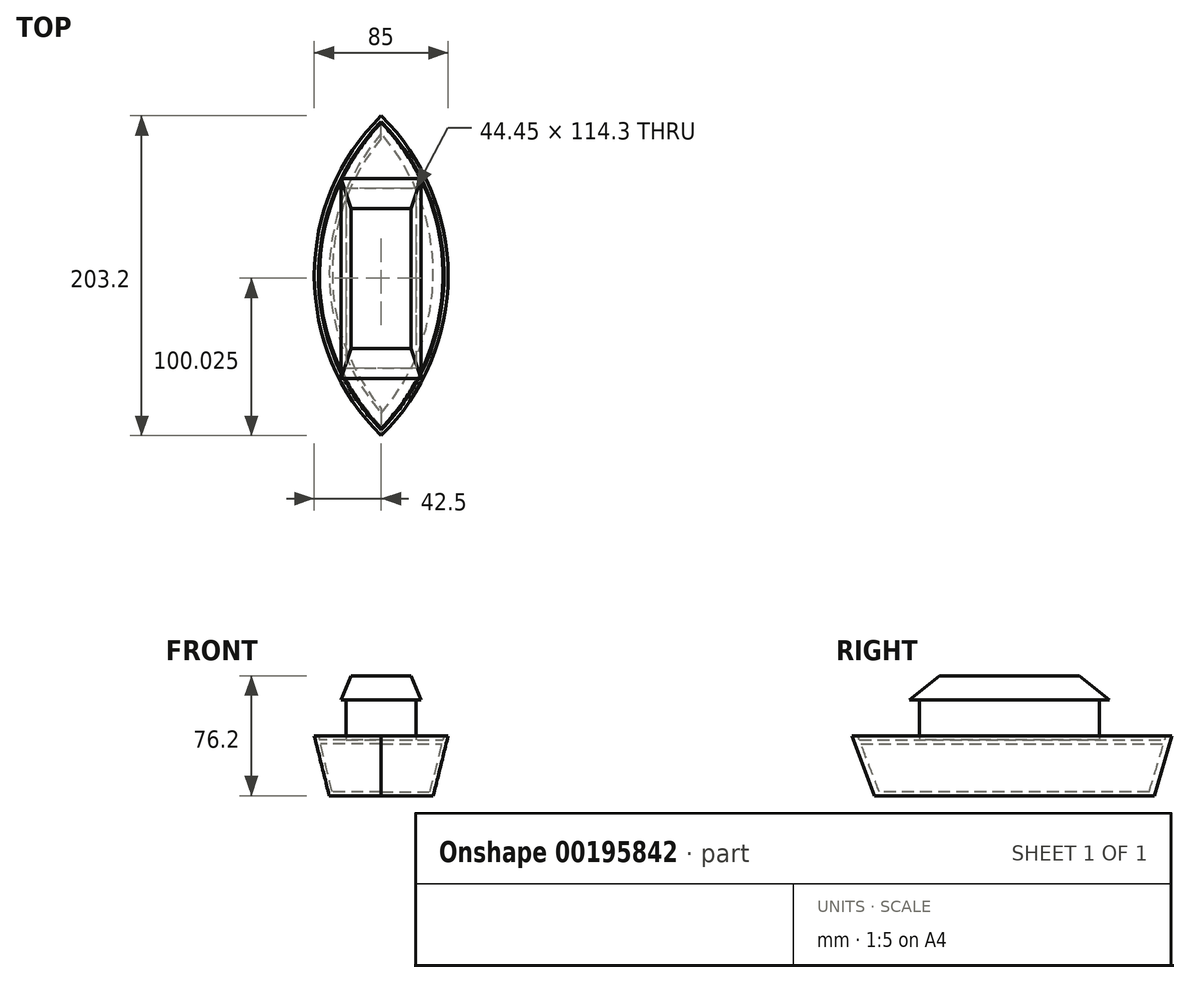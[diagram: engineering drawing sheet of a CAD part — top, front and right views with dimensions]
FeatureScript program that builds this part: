
annotation { "Feature Type Name" : "Feature", "Feature Type Description" : "" }
export const myFeature = defineFeature(function(context is Context, id is Id, definition is map)
    precondition{}
    {
        {
            var Q0;
            Q0=qCreatedBy(makeId("Top.planeOp"),FACE);
            var sketch = newSketch(context, id + "F0", { "sketchPlane" : qUnion([Q0])});
            skArc(sketch, "E0", {"start": v(0, -98.62) * mm, "mid": v(33.06, -9.72) * mm, "end": v(0, 79.18) * mm});
            skArc(sketch, "E1.MirrorCS", {"start": v(0, -98.62) * mm, "mid": v(-33.06, -9.72) * mm, "end": v(0, 79.18) * mm});
            skSolve(sketch);
        }
        {
            var Q0;
            Q0=qCreatedBy(makeId("Top.planeOp"),FACE);
            cPlane(context, id + "F1", {"entities" : qUnion([Q0]), "cplaneType" : CPlaneType.OFFSET, "offset" : 38.1 * mm, "width" : 152.4 * mm, "height" : 152.4 * mm});
        }
        {
            var Q0;
            Q0=qCreatedBy(id+"F1.planeOp",FACE);
            var sketch = newSketch(context, id + "F2", { "sketchPlane" : qUnion([Q0])});
            skArc(sketch, "E2", {"start": v(0, -112.85) * mm, "mid": v(42.5, -11.25) * mm, "end": v(0, 90.35) * mm});
            skArc(sketch, "E3.MirrorCS", {"start": v(0, -112.85) * mm, "mid": v(-42.5, -11.25) * mm, "end": v(0, 90.35) * mm});
            skSolve(sketch);
        }
        {
            var Q0;
            Q0=makeQuery(id+"F0.imprint","IMPRINT",FACE,{"disambiguationData":[TD([[makeQuery(id+"F0.imprint","IMPRINT",EDGE,{"derivedFrom":sQuery(id+"F0.wireOp",EDGE,"E0")}),1.0]])]});
            var Q1;
            Q1=makeQuery(id+"F2.imprint","IMPRINT",FACE,{"disambiguationData":[TD([[makeQuery(id+"F2.imprint","IMPRINT",EDGE,{"derivedFrom":sQuery(id+"F2.wireOp",EDGE,"E2")}),1.0]])]});
            loft(context, id + "F3", {"sheetProfilesArray" : [{ "sheetProfileEntities" : qUnion([Q0]) }, { "sheetProfileEntities" : qUnion([Q1]) }]});
        }
        {
            var Q0;
            Q0=makeQuery(id+"F3.opLoft","CAP_FACE",FACE,{"disambiguationData":[OSD([makeQuery(id+"F2.imprint","IMPRINT",FACE,{"disambiguationData":[TD([[makeQuery(id+"F2.imprint","IMPRINT",EDGE,{"derivedFrom":sQuery(id+"F2.wireOp",EDGE,"E2")}),1.0]])]})])],"isStart":true});
            shell(context, id + "F4", {"entities" : qUnion([Q0]), "thickness" : 2.54 * mm});
        }
        {
            var Q0;
            Q0=qCreatedBy(id+"F1.planeOp",FACE);
            cPlane(context, id + "F5", {"entities" : qUnion([Q0]), "cplaneType" : CPlaneType.OFFSET, "offset" : 2.54 * mm, "oppositeDirection" : true, "width" : 152.4 * mm, "height" : 152.4 * mm});
        }
        {
            var Q0;
            Q0=qCreatedBy(id+"F5.planeOp",FACE);
            var sketch = newSketch(context, id + "F6", { "sketchPlane" : qUnion([Q0])});
            skPoint(sketch, "E4", {"position": v(0, 87.4) * mm});
            skPoint(sketch, "E5", {"position": v(0, -109.13) * mm});
            skArc(sketch, "E6", {"start": v(0, -109.13) * mm, "mid": v(39.52, -10.86) * mm, "end": v(0, 87.4) * mm});
            skArc(sketch, "E7", {"start": v(0, 87.4) * mm, "mid": v(-40.42, -10.86) * mm, "end": v(0, -109.13) * mm});
            skSolve(sketch);
        }
        {
            var Q0;
            Q0=makeQuery(id+"F6.imprint","IMPRINT",FACE,{"disambiguationData":[TD([[makeQuery(id+"F6.imprint","IMPRINT",EDGE,{"derivedFrom":sQuery(id+"F6.wireOp",EDGE,"E6")}),1.0]])]});
            extrude(context, id + "F7", {"entities" : qUnion([Q0]), "operationType" : NewBodyOperationType.ADD, "oppositeDirection" : true, "depth" : 2.54 * mm});
        }
        {
            var Q0;
            Q0=qCreatedBy(id+"F5.planeOp",FACE);
            var sketch = newSketch(context, id + "F8", { "sketchPlane" : qUnion([Q0])});
            skLineSegment(sketch, "E8.bottom", {"start": v(-22.23, 44.32) * mm, "end": v(22.23, 44.32) * mm});
            skLineSegment(sketch, "E8.top", {"start": v(-22.23, -69.98) * mm, "end": v(22.22, -69.98) * mm});
            skLineSegment(sketch, "E8.left", {"start": v(-22.23, 44.32) * mm, "end": v(-22.23, -69.98) * mm});
            skLineSegment(sketch, "E8.right", {"start": v(22.23, 44.32) * mm, "end": v(22.22, -69.98) * mm});
            skPoint(sketch, "E8.middle", {"position": v(0, -12.83) * mm});
            skSolve(sketch);
        }
        {
            var Q0;
            Q0=makeQuery(id+"F8.imprint","IMPRINT",FACE,{"disambiguationData":[TD([[makeQuery(id+"F8.imprint","IMPRINT",EDGE,{"derivedFrom":sQuery(id+"F8.wireOp",EDGE,"E8.bottom")}),-1.0]])]});
            extrude(context, id + "F9", {"entities" : qUnion([Q0]), "operationType" : NewBodyOperationType.ADD, "depth" : 25.4 * mm});
        }
        {
            var Q0;
            Q0=qCreatedBy(id+"F1.planeOp",FACE);
            cPlane(context, id + "F10", {"entities" : qUnion([Q0]), "cplaneType" : CPlaneType.OFFSET, "offset" : 38.1 * mm, "width" : 152.4 * mm, "height" : 152.4 * mm});
        }
        {
            var Q0;
            Q0=qCreatedBy(id+"F10.planeOp",FACE);
            var sketch = newSketch(context, id + "F11", { "sketchPlane" : qUnion([Q0])});
            skLineSegment(sketch, "E9.bottom", {"start": v(-19.05, 31.51) * mm, "end": v(19.05, 31.51) * mm});
            skLineSegment(sketch, "E9.top", {"start": v(-19.05, -57.39) * mm, "end": v(19.05, -57.39) * mm});
            skLineSegment(sketch, "E9.left", {"start": v(-19.05, 31.51) * mm, "end": v(-19.05, -57.39) * mm});
            skLineSegment(sketch, "E9.right", {"start": v(19.05, 31.51) * mm, "end": v(19.05, -57.39) * mm});
            skPoint(sketch, "E9.middle", {"position": v(0, -12.94) * mm});
            skSolve(sketch);
        }
        {
            var Q0;
            Q0=qCreatedBy(id+"F10.planeOp",FACE);
            cPlane(context, id + "F12", {"entities" : qUnion([Q0]), "cplaneType" : CPlaneType.OFFSET, "offset" : 15.24 * mm, "oppositeDirection" : true, "width" : 152.4 * mm, "height" : 152.4 * mm});
        }
        {
            var Q0;
            Q0=qCreatedBy(id+"F12.planeOp",FACE);
            var sketch = newSketch(context, id + "F13", { "sketchPlane" : qUnion([Q0])});
            skLineSegment(sketch, "E10.bottom", {"start": v(-25.4, 50.52) * mm, "end": v(25.4, 50.52) * mm});
            skLineSegment(sketch, "E10.top", {"start": v(-25.4, -76.48) * mm, "end": v(25.4, -76.48) * mm});
            skLineSegment(sketch, "E10.left", {"start": v(-25.4, 50.52) * mm, "end": v(-25.4, -76.48) * mm});
            skLineSegment(sketch, "E10.right", {"start": v(25.4, 50.52) * mm, "end": v(25.4, -76.48) * mm});
            skPoint(sketch, "E10.middle", {"position": v(0, -12.98) * mm});
            skSolve(sketch);
        }
        {
            var Q1;
            Q1=makeQuery(id+"F13.imprint","IMPRINT",FACE,{"disambiguationData":[TD([[makeQuery(id+"F13.imprint","IMPRINT",EDGE,{"derivedFrom":sQuery(id+"F13.wireOp",EDGE,"E10.bottom")}),-1.0]])]});
            var Q2;
            Q2=makeQuery(id+"F11.imprint","IMPRINT",FACE,{"disambiguationData":[TD([[makeQuery(id+"F11.imprint","IMPRINT",EDGE,{"derivedFrom":sQuery(id+"F11.wireOp",EDGE,"E9.bottom")}),-1.0]])]});
            loft(context, id + "F14", {"operationType" : NewBodyOperationType.ADD, "sheetProfilesArray" : [{ "sheetProfileEntities" : qUnion([Q1]) }, { "sheetProfileEntities" : qUnion([Q2]) }]});
        }
    });
